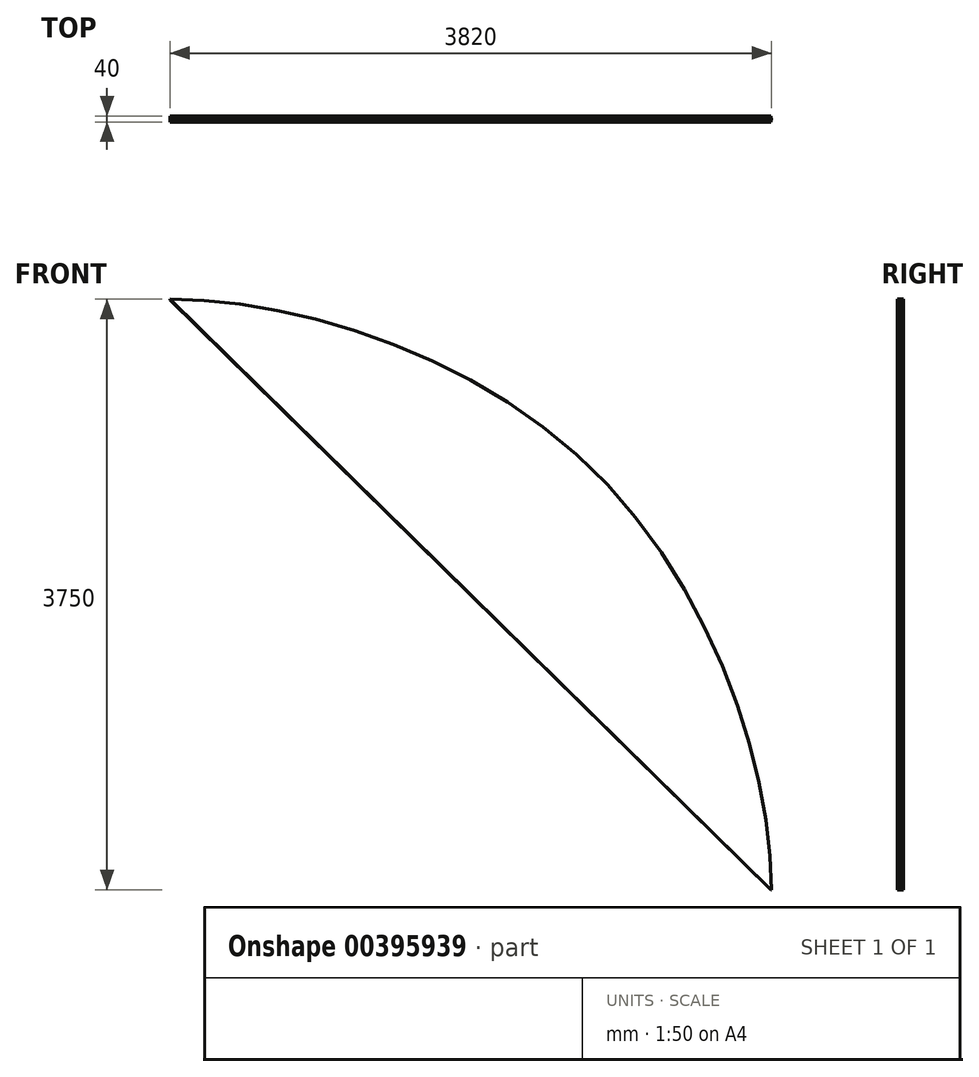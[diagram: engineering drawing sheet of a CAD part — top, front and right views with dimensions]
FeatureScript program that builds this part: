
annotation { "Feature Type Name" : "Feature", "Feature Type Description" : "" }
export const myFeature = defineFeature(function(context is Context, id is Id, definition is map)
    precondition{}
    {
        {
            var Q0;
            Q0=qCreatedBy(makeId("Front.planeOp"),FACE);
            var sketch = newSketch(context, id + "F0", { "sketchPlane" : qUnion([Q0])});
            skFitSpline(sketch, "E0", {"points": [v(0, 3750) * mm, v(2676.4, 2676.4) * mm, v(3820, 0) * mm], "startDerivative": vector(4811.12, 0) * mm, "endDerivative": vector(0, -4788.93) * mm});
            skLineSegment(sketch, "E1", {"start": v(2676.4, 2676.4) * mm, "end": v(0, 0) * mm, "construction": true});
            skLineSegment(sketch, "E2", {"start": v(0, 0) * mm, "end": v(0, 3750) * mm, "construction": true});
            skSolve(sketch);
        }
        {
            var Q0;
            Q0=qCreatedBy(makeId("Right.planeOp"),FACE);
            var sketch = newSketch(context, id + "F1", { "sketchPlane" : qUnion([Q0])});
            skLineSegment(sketch, "E3", {"start": v(0, 3750) * mm, "end": v(-20, 3750) * mm});
            skLineSegment(sketch, "E4", {"start": v(-20, 3750) * mm, "end": v(-20, 3746) * mm});
            skLineSegment(sketch, "E5", {"start": v(-20, 3746) * mm, "end": v(20, 3746) * mm});
            skLineSegment(sketch, "E6", {"start": v(20, 3746) * mm, "end": v(20, 3750) * mm});
            skLineSegment(sketch, "E7", {"start": v(20, 3750) * mm, "end": v(0, 3750) * mm});
            skSolve(sketch);
        }
        {
            var Q0;
            Q0=qCreatedBy(makeId("Top.planeOp"),FACE);
            var sketch = newSketch(context, id + "F2", { "sketchPlane" : qUnion([Q0])});
            skLineSegment(sketch, "E8", {"start": v(3820, 0) * mm, "end": v(3816, -20) * mm});
            skLineSegment(sketch, "E9", {"start": v(3816, 20) * mm, "end": v(3820, 0) * mm});
            skLineSegment(sketch, "E10", {"start": v(3820, 0) * mm, "end": v(3816, 0) * mm, "construction": true});
            skLineSegment(sketch, "E11", {"start": v(3816, -20) * mm, "end": v(3816, 0) * mm});
            skLineSegment(sketch, "E12", {"start": v(3816, 0) * mm, "end": v(3816, 20) * mm});
            skSolve(sketch);
        }
        {
            var Q0;
            Q0 = qSketchRegion(id + "F1", true);
            var Q1;
            Q1 = qSketchRegion(id + "F2", true);
            var Q2;
            Q2 = qConstructionFilter(qBodyType(qCreatedBy(id + "F0" ,EDGE), BodyType.WIRE), ConstructionObject.NO);
            loft(context, id + "F3", {"addGuides" : true, "sheetProfilesArray" : [{ "sheetProfileEntities" : qUnion([Q0]) }, { "sheetProfileEntities" : qUnion([Q1]) }], "guidesArray" : [{ "guideEntities" : qUnion([Q2]), "guideDerivativeType" : LoftGuideDerivativeType.DEFAULT, "guideDerivativeMagnitude" : 1 }]});
        }
    });
